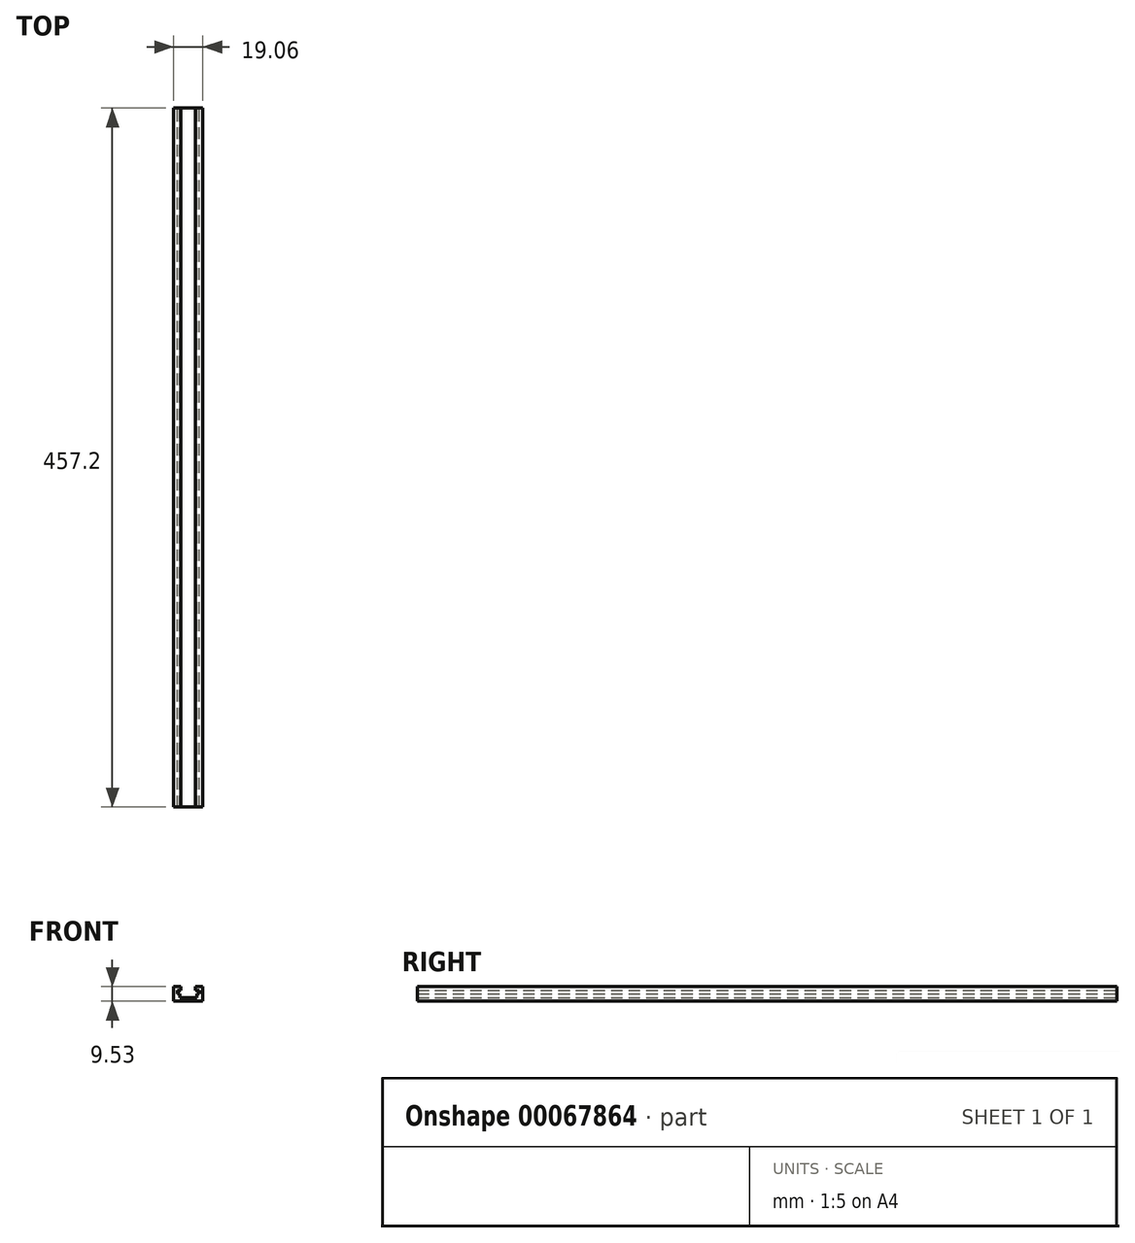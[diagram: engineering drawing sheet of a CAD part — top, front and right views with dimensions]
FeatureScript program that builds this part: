
annotation { "Feature Type Name" : "Feature", "Feature Type Description" : "" }
export const myFeature = defineFeature(function(context is Context, id is Id, definition is map)
    precondition{}
    {
        {
            var Q0;
            Q0=qCreatedBy(makeId("Front.planeOp"),FACE);
            var sketch = newSketch(context, id + "F0", { "sketchPlane" : qUnion([Q0])});
            skLineSegment(sketch, "E0", {"start": v(-4.76, 9.53) * mm, "end": v(-9.52, 9.53) * mm});
            skLineSegment(sketch, "E1", {"start": v(-9.52, 9.53) * mm, "end": v(-9.52, 0) * mm});
            skLineSegment(sketch, "E2", {"start": v(-9.52, 0) * mm, "end": v(9.52, 0) * mm});
            skLineSegment(sketch, "E3", {"start": v(9.53, 0) * mm, "end": v(9.53, 9.53) * mm});
            skLineSegment(sketch, "E4", {"start": v(9.52, 9.53) * mm, "end": v(4.76, 9.53) * mm});
            skLineSegment(sketch, "E5", {"start": v(4.76, 9.53) * mm, "end": v(4.76, 7.14) * mm});
            skLineSegment(sketch, "E6", {"start": v(4.76, 7.14) * mm, "end": v(7.14, 7.14) * mm});
            skLineSegment(sketch, "E7", {"start": v(7.14, 7.14) * mm, "end": v(7.14, 4.76) * mm});
            skLineSegment(sketch, "E8", {"start": v(7.14, 4.76) * mm, "end": v(5.56, 4.76) * mm});
            skLineSegment(sketch, "E9", {"start": v(5.56, 4.76) * mm, "end": v(5.56, 2.38) * mm});
            skLineSegment(sketch, "E10", {"start": v(5.56, 2.38) * mm, "end": v(-5.56, 2.38) * mm});
            skLineSegment(sketch, "E11", {"start": v(-5.56, 2.38) * mm, "end": v(-5.56, 4.76) * mm});
            skLineSegment(sketch, "E12", {"start": v(-5.56, 4.76) * mm, "end": v(-7.14, 4.76) * mm});
            skLineSegment(sketch, "E13", {"start": v(-7.14, 4.76) * mm, "end": v(-7.14, 7.14) * mm});
            skLineSegment(sketch, "E14", {"start": v(-7.14, 7.14) * mm, "end": v(-4.76, 7.14) * mm});
            skLineSegment(sketch, "E15", {"start": v(-4.76, 7.14) * mm, "end": v(-4.76, 9.53) * mm});
            skLineSegment(sketch, "E16", {"start": v(0, -39.54) * mm, "end": v(0, 31.07) * mm, "construction": true});
            skSolve(sketch);
        }
        {
            var Q0;
            Q0=makeQuery(id+"F0.imprint","IMPRINT",FACE,{"disambiguationData":[TD([[makeQuery(id+"F0.imprint","IMPRINT",EDGE,{"derivedFrom":sQuery(id+"F0.wireOp",EDGE,"E0")}),1.0]])]});
            extrude(context, id + "F1", {"entities" : qUnion([Q0]), "endBound" : BoundingType.SYMMETRIC, "depth" : 457.2 * mm});
        }
    });
